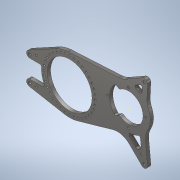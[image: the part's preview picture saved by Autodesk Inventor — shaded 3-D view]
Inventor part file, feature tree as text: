
AUTODESK INVENTOR PART (.ipt)
format: ipt  version: 2021 (Build 250183000, 183)  size: 499,200 bytes
history: native  units: in
note: dims shown in document units (in); Inventor stores cm internally (conversion verified against a paired STEP export)
features: sketch x13, extrude x10, hole x3, projected_geometry x3, fillet x2, chamfer x1
ambient origin geometry x8: Origin, YZ Plane, XZ Plane, XY Plane, X Axis, Y Axis, Z Axis, Center Point
bodies: Body1 (feature_tree)
feature tree (32):
  extrude  "Extrusion24"  Depth=2.16in
  extrude  "Extrusion28"  Depth=9.0in
  hole  "Hole9"  [1 undecoded]
  hole  "Hole11"  [1 undecoded]
  hole  "Hole13"  [1 undecoded]
  extrude  "Extrusion30"  Depth=1.5in
  extrude  "Extrusion31"  Depth=0.5in
  extrude  "Extrusion32"  Depth=0.25in
  extrude  "Extrusion33"  Depth=7.75in
  extrude  "Extrusion34"  Depth=0.25in
  chamfer  "Chamfer2"  Distance=1.0in
  sketch  "Sketch58"  dims[d291=3.5433in d293=360.0deg]
  extrude  "Extrusion42"  Depth=0.5in
  extrude  "Extrusion43"  Depth=0.5in
  fillet  "Fillet4"  Radius=0.3972in
  extrude  "Extrusion44"  Depth=0.5in
  fillet  "Fillet5"  Radius=0.1355in
  sketch  "Sketch2"  dims[d9=8.5in d92=2.16in]
  sketch  "Sketch35"  dims[d118=0.75in d119=0.75in d120=0.75in d121=0.75in d137=9.0in d142=6.5in]
  projected_geometry  "Projected Loop2"
  sketch  "Sketch36"  dims[d143=1.0in d210=1.0in]
  sketch  "Sketch40"  dims[d211=6.0in d212=6.0in]
  sketch  "Sketch43"  dims[d213=3.718in d214=1.0in]
  sketch  "Sketch46"  dims[d235=10.718in d237=1.5in]
  sketch  "Sketch47"  dims[d239=0.5in d240=0.0in d266=6.75in]
  sketch  "Sketch48"  dims[d267=0.5in d268=0.0in]
  sketch  "Sketch49"  dims[d269=0.386in d270=0.75in d271=0.762in d272=0.25in d273=0.5635in d274=0.484in d275=0.8108in d288=5.0in]
  sketch  "Sketch50"  dims[d289=17.223in d290=7.75in]
  sketch  "Sketch64"  dims[d295=0.257in d296=0.75in d297=0.438in d298=0.25in d299=0.5635in d300=1.0in d301=0.8108in d302=0.1718in]
  sketch  "Sketch65"  dims[d303=15.0deg d316=1.0in d317=0.0481in d318=1.0in d319=0.3972in d322=0.271in d323=0.1355in d324=0.5in d325=0.266in d326=0.75in d327=0.507in d328=0.25in d329=0.5635in d330=1.0in d331=0.8108in d346=3.0in d347=1.0in d348=0.0in d349=0.75in d350=0.75in d351=0.5in d353=0.75in d354=0.75in d355=0.25in d356=1.0in d357=0.0in d358=0.25in d359=1.0in d360=0.0in d361=1.0in d362=1.0in d363=0.25in d364=1.0in d365=0.0in d366=2.5in d367=1.0in d368=0.0in d373=0.0156in d374=0.125in d375=45.0deg d435=1.0in d436=0.0in d437=5.75in d438=30.0deg d439=1.0in d440=0.0in d442=0.25in d443=5.25in d444=0.325in d445=1.5748in d447=360.0deg d449=1.0in d450=0.0in d451=0.25in d452=0.5in d453=0.325in]
  projected_geometry  "Project Cut Edges2"
  projected_geometry  "Project Cut Edges4"
note: 3 required parameter values undecoded (feature->parameter linkage not recoverable at this tier; creation-order binding heuristic only, values carry confidence <= 0.55)
